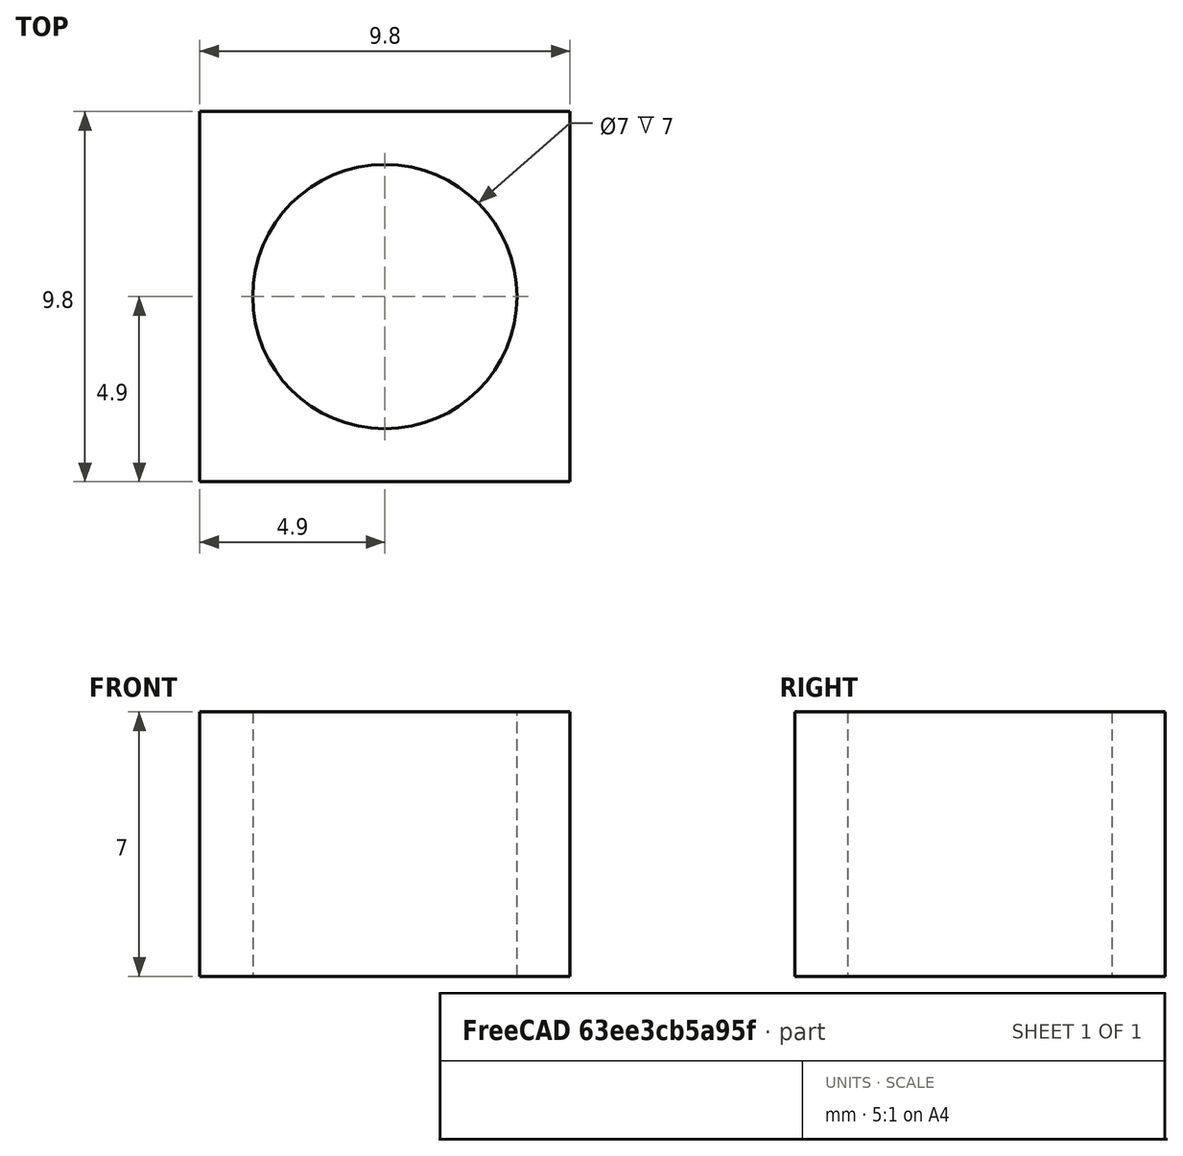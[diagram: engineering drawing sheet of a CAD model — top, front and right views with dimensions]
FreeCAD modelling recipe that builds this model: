
FCSTD DOCUMENT  (FreeCAD 0.16R6706 (Git))
Label: Spacer
License: All rights reserved
LicenseURL: http://en.wikipedia.org/wiki/All_rights_reserved
objects: Sketcher::SketchObject×1, PartDesign::Pad×1
note: 3 computed .brp shape members not serialized (recipe doc carries the construction recipe); baked Part::Feature solids carry a one-line shape summary decoded from their .brp

FEATURE [Sketcher::SketchObject] Sketch
  sketch-geometry (5):
    g0: LineSegment StartX=4.9 StartY=4.9 StartZ=0 EndX=-4.9 EndY=4.9 EndZ=0
    g1: LineSegment StartX=-4.9 StartY=4.9 StartZ=0 EndX=-4.9 EndY=-4.9 EndZ=0
    g2: LineSegment StartX=-4.9 StartY=-4.9 StartZ=0 EndX=4.9 EndY=-4.9 EndZ=0
    g3: LineSegment StartX=4.9 StartY=-4.9 StartZ=0 EndX=4.9 EndY=4.9 EndZ=0
    g4: Circle CenterX=0 CenterY=0 CenterZ=0 NormalX=0 NormalY=0 NormalZ=1 Radius=3.5
  constraints (13):
    c: Coincident(g0,g1)
    c: Coincident(g1,g2)
    c: Coincident(g2,g3)
    c: Coincident(g3,g0)
    c: Horizontal(g0)
    c: Horizontal(g2)
    c: Vertical(g1)
    c: Vertical(g3)
    c: Symmetric(g1,g0,g-1)
    c: Equal(g2,g3)
    c: DistanceY(g3,g3) = 9.8
    c: Coincident(g4,g-1)
    c: Radius(g4) = 3.5
FEATURE [PartDesign::Pad] Pad
  Length = 7
  Length2 = 100
  Sketch = -> Sketch
  Type = 0
